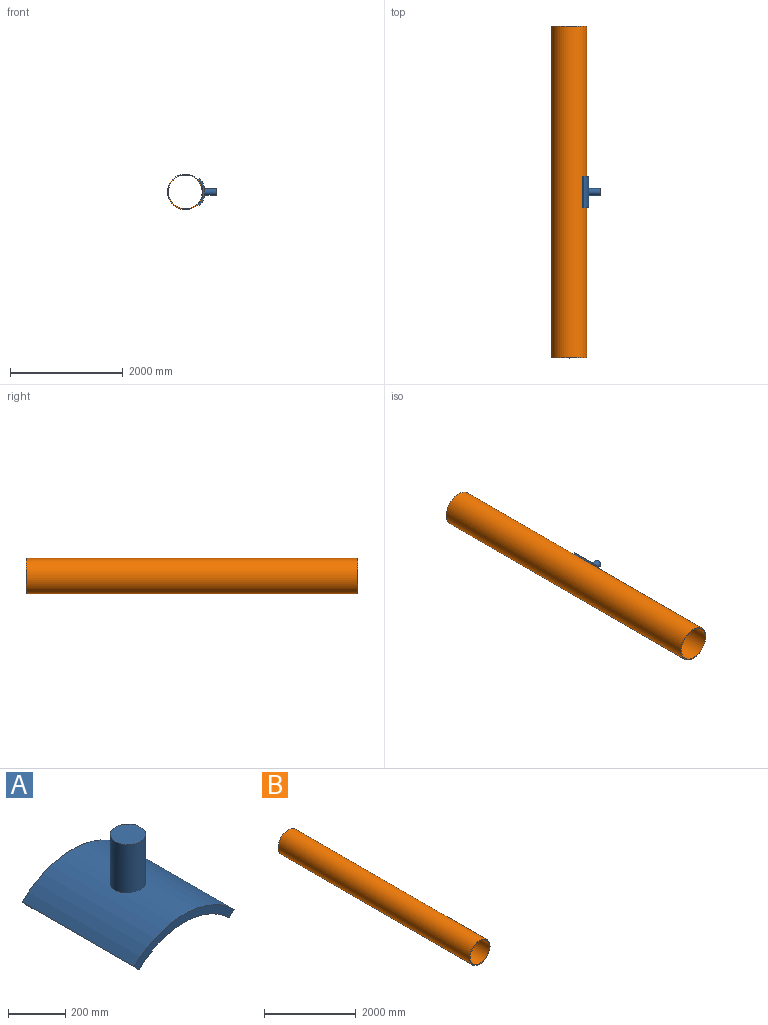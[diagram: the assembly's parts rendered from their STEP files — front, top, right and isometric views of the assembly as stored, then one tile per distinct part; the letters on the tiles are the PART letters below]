
ASSEMBLY  parts=2 mates=1
PART A: 8 faces, bbox 495x556x331.3 mm
  f0: plane 556x24.75mm, normal (0.71,0,-0.71), area 19460mm2, adj f1,f3,f4,f5
  f1: cylinder r=350mm len=556mm, axis (0,-1,0), area 293357.8mm2, adj f0,f2,f4,f5,f6
  f2: plane 556x24.75mm, normal (-0.71,0,-0.71), area 19460mm2, adj f1,f3,f4,f5
  f3: cylinder r=315mm len=556mm, axis (0,-1,0), area 275109.3mm2, adj f0,f2,f4,f5
  f4: plane 494.97x127.26mm, normal (0,1,0), area 18280.1mm2, adj f0,f1,f2,f3
  f5: plane 494.97x127.26mm, normal (0,-1,0), area 18280.1mm2, adj f0,f1,f2,f3
  f6: cylinder r=62.5mm len=209.63mm, axis (0,0,1), area 81211.9mm2, adj f1,f7
  f7: plane 125x125mm, normal (0,0,1), area 12271.8mm2, adj f6
PART B: 4 faces, bbox 630x5900x630 mm
  f0: cylinder r=300mm len=5900mm, axis (0,1,0), area 11121238mm2, adj f2,f3
  f1: cylinder r=315mm len=5900mm, axis (0,1,0), area 11677299.9mm2, adj f2,f3
  f2: plane 630x630mm, normal (0,-1,0), area 28981.2mm2, adj f0,f1
  f3: plane 630x630mm, normal (0,1,0), area 28981.2mm2, adj f0,f1
PLACE A rot(axis=(0,1,0),90deg) t=(1522.75,1500.63,-3.04)mm
PLACE B t=(7.75,-54.37,1511.96)mm
MATE cylindrical A.f3 <-> B.f0  axis (0,-1,0) through (7.75,-54.37,-3.04)mm
